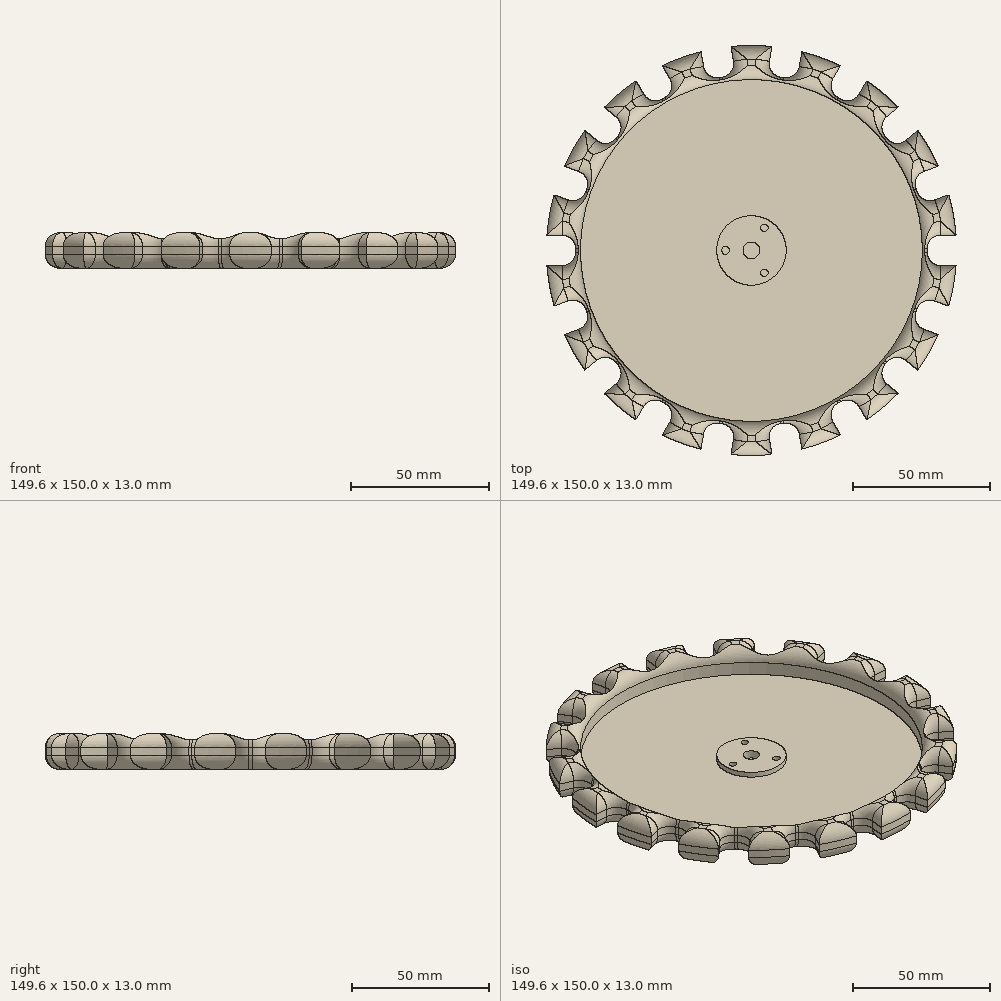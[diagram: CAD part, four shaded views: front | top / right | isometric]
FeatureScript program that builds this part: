
annotation { "Feature Type Name" : "Feature", "Feature Type Description" : "" }
export const myFeature = defineFeature(function(context is Context, id is Id, definition is map)
    precondition{}
    {
        {
            var Q0;
            Q0=qCreatedBy(makeId("Top.planeOp"),FACE);
            var sketch = newSketch(context, id + "F0", { "sketchPlane" : qUnion([Q0])});
            skCircle(sketch, "E0", {"center": v(0, 0) * mm, "radius": 75 * mm});
            skCircle(sketch, "E1", {"center": v(0, 0) * mm, "radius": 62.5 * mm});
            skLineSegment(sketch, "E2", {"start": v(0, 0) * mm, "end": v(-124.02, 0) * mm, "construction": true});
            skPoint(sketch, "E3", {"position": v(-75, 0) * mm});
            skLineSegment(sketch, "E4.bottom", {"start": v(-75.75, -5.55) * mm, "end": v(-69.25, -5.55) * mm});
            skLineSegment(sketch, "E4.top", {"start": v(-75.75, 5.55) * mm, "end": v(-69.25, 5.55) * mm});
            skLineSegment(sketch, "E4.left", {"start": v(-75.75, -5.55) * mm, "end": v(-75.75, 5.55) * mm});
            skLineSegment(sketch, "E4.right", {"start": v(-64.25, -0.55) * mm, "end": v(-64.25, 0.55) * mm});
            skPoint(sketch, "E4.middle", {"position": v(-70, 0) * mm});
            skPoint(sketch, "E5.visualSharp", {"position": v(-64.25, 5.55) * mm});
            skArc(sketch, "E5.filletArc", {"start": v(-64.25, 0.55) * mm, "mid": v(-65.71, 4.09) * mm, "end": v(-69.25, 5.55) * mm});
            skPoint(sketch, "E6.visualSharp", {"position": v(-64.25, -5.55) * mm});
            skArc(sketch, "E6.filletArc", {"start": v(-69.25, -5.55) * mm, "mid": v(-65.71, -4.09) * mm, "end": v(-64.25, -0.55) * mm});
            skPoint(sketch, "E7.center", {"position": v(1.56, 0) * mm});
            skCircle(sketch, "E8", {"center": v(0, 0) * mm, "radius": 3.05 * mm});
            skCircle(sketch, "E9", {"center": v(0, 0) * mm, "radius": 12.7 * mm});
            skCircle(sketch, "E10", {"center": v(0, 0) * mm, "radius": 9.5 * mm, "construction": true});
            skCircle(sketch, "E11", {"center": v(-9.5, 0) * mm, "radius": 1.4 * mm});
            skCircle(sketch, "E12.1.0", {"center": v(-4.75, -8.23) * mm, "radius": 1.4 * mm});
            skCircle(sketch, "E12.2.0", {"center": v(4.75, -8.23) * mm, "radius": 1.4 * mm});
            skCircle(sketch, "E12.3.0", {"center": v(9.5, 0) * mm, "radius": 1.4 * mm});
            skCircle(sketch, "E12.4.0", {"center": v(4.75, 8.23) * mm, "radius": 1.4 * mm});
            skCircle(sketch, "E12.5.0", {"center": v(-4.75, 8.23) * mm, "radius": 1.4 * mm});
            skPoint(sketch, "E13.1.0", {"position": v(-62.27, -16.76) * mm});
            skPoint(sketch, "E13.1.1", {"position": v(-70.48, -25.65) * mm});
            skPoint(sketch, "E13.1.2", {"position": v(-58.48, -27.2) * mm});
            skPoint(sketch, "E13.1.3", {"position": v(-65.78, -23.94) * mm});
            skArc(sketch, "E13.1.4", {"start": v(-63.18, -28.9) * mm, "mid": v(-60.35, -26.31) * mm, "end": v(-60.19, -22.5) * mm});
            skArc(sketch, "E13.1.5", {"start": v(-60.56, -21.46) * mm, "mid": v(-63.15, -18.64) * mm, "end": v(-66.97, -18.47) * mm});
            skLineSegment(sketch, "E13.1.6", {"start": v(-69.28, -31.12) * mm, "end": v(-73.08, -20.7) * mm});
            skLineSegment(sketch, "E13.1.7", {"start": v(-60.19, -22.5) * mm, "end": v(-60.56, -21.46) * mm});
            skLineSegment(sketch, "E13.1.8", {"start": v(-73.08, -20.7) * mm, "end": v(-66.97, -18.47) * mm});
            skLineSegment(sketch, "E13.1.9", {"start": v(-69.28, -31.12) * mm, "end": v(-63.18, -28.9) * mm});
            skPoint(sketch, "E13.2.0", {"position": v(-52.79, -37.05) * mm});
            skPoint(sketch, "E13.2.1", {"position": v(-57.45, -48.2) * mm});
            skPoint(sketch, "E13.2.2", {"position": v(-45.65, -45.55) * mm});
            skPoint(sketch, "E13.2.3", {"position": v(-53.62, -45) * mm});
            skArc(sketch, "E13.2.4", {"start": v(-49.48, -48.76) * mm, "mid": v(-47.71, -45.37) * mm, "end": v(-48.86, -41.72) * mm});
            skArc(sketch, "E13.2.5", {"start": v(-49.57, -40.88) * mm, "mid": v(-52.97, -39.11) * mm, "end": v(-56.62, -40.26) * mm});
            skLineSegment(sketch, "E13.2.6", {"start": v(-54.46, -52.94) * mm, "end": v(-61.6, -44.44) * mm});
            skLineSegment(sketch, "E13.2.7", {"start": v(-48.86, -41.72) * mm, "end": v(-49.57, -40.88) * mm});
            skLineSegment(sketch, "E13.2.8", {"start": v(-61.6, -44.44) * mm, "end": v(-56.62, -40.26) * mm});
            skLineSegment(sketch, "E13.2.9", {"start": v(-54.46, -52.94) * mm, "end": v(-49.48, -48.76) * mm});
            skPoint(sketch, "E13.3.0", {"position": v(-36.93, -52.87) * mm});
            skPoint(sketch, "E13.3.1", {"position": v(-37.5, -64.95) * mm});
            skPoint(sketch, "E13.3.2", {"position": v(-27.32, -58.42) * mm});
            skPoint(sketch, "E13.3.3", {"position": v(-35, -60.62) * mm});
            skArc(sketch, "E13.3.4", {"start": v(-29.82, -62.75) * mm, "mid": v(-29.32, -58.95) * mm, "end": v(-31.65, -55.92) * mm});
            skArc(sketch, "E13.3.5", {"start": v(-32.6, -55.37) * mm, "mid": v(-36.4, -54.87) * mm, "end": v(-39.43, -57.2) * mm});
            skLineSegment(sketch, "E13.3.6", {"start": v(-33.07, -68.38) * mm, "end": v(-42.68, -62.83) * mm});
            skLineSegment(sketch, "E13.3.7", {"start": v(-31.65, -55.92) * mm, "end": v(-32.6, -55.37) * mm});
            skLineSegment(sketch, "E13.3.8", {"start": v(-42.68, -62.83) * mm, "end": v(-39.43, -57.2) * mm});
            skLineSegment(sketch, "E13.3.9", {"start": v(-33.07, -68.38) * mm, "end": v(-29.82, -62.75) * mm});
            skPoint(sketch, "E13.4.0", {"position": v(-16.62, -62.31) * mm});
            skPoint(sketch, "E13.4.1", {"position": v(-13.02, -73.86) * mm});
            skPoint(sketch, "E13.4.2", {"position": v(-5.7, -64.24) * mm});
            skPoint(sketch, "E13.4.3", {"position": v(-12.16, -68.94) * mm});
            skArc(sketch, "E13.4.4", {"start": v(-6.56, -69.16) * mm, "mid": v(-7.39, -65.43) * mm, "end": v(-10.62, -63.37) * mm});
            skArc(sketch, "E13.4.5", {"start": v(-11.7, -63.18) * mm, "mid": v(-15.43, -64) * mm, "end": v(-17.5, -67.23) * mm});
            skLineSegment(sketch, "E13.4.6", {"start": v(-7.69, -75.56) * mm, "end": v(-18.62, -73.64) * mm});
            skLineSegment(sketch, "E13.4.7", {"start": v(-10.62, -63.37) * mm, "end": v(-11.7, -63.18) * mm});
            skLineSegment(sketch, "E13.4.8", {"start": v(-18.62, -73.64) * mm, "end": v(-17.5, -67.23) * mm});
            skLineSegment(sketch, "E13.4.9", {"start": v(-7.69, -75.56) * mm, "end": v(-6.56, -69.16) * mm});
            skPoint(sketch, "E13.5.0", {"position": v(5.7, -64.24) * mm});
            skPoint(sketch, "E13.5.1", {"position": v(13.02, -73.86) * mm});
            skPoint(sketch, "E13.5.2", {"position": v(16.62, -62.31) * mm});
            skPoint(sketch, "E13.5.3", {"position": v(12.16, -68.94) * mm});
            skArc(sketch, "E13.5.4", {"start": v(17.5, -67.23) * mm, "mid": v(15.43, -64) * mm, "end": v(11.7, -63.18) * mm});
            skArc(sketch, "E13.5.5", {"start": v(10.62, -63.37) * mm, "mid": v(7.39, -65.43) * mm, "end": v(6.56, -69.16) * mm});
            skLineSegment(sketch, "E13.5.6", {"start": v(18.62, -73.64) * mm, "end": v(7.69, -75.56) * mm});
            skLineSegment(sketch, "E13.5.7", {"start": v(11.7, -63.18) * mm, "end": v(10.62, -63.37) * mm});
            skLineSegment(sketch, "E13.5.8", {"start": v(7.69, -75.56) * mm, "end": v(6.56, -69.16) * mm});
            skLineSegment(sketch, "E13.5.9", {"start": v(18.62, -73.64) * mm, "end": v(17.5, -67.23) * mm});
            skPoint(sketch, "E13.6.0", {"position": v(27.32, -58.42) * mm});
            skPoint(sketch, "E13.6.1", {"position": v(37.5, -64.95) * mm});
            skPoint(sketch, "E13.6.2", {"position": v(36.93, -52.87) * mm});
            skPoint(sketch, "E13.6.3", {"position": v(35, -60.62) * mm});
            skArc(sketch, "E13.6.4", {"start": v(39.43, -57.2) * mm, "mid": v(36.4, -54.87) * mm, "end": v(32.6, -55.37) * mm});
            skArc(sketch, "E13.6.5", {"start": v(31.65, -55.92) * mm, "mid": v(29.32, -58.95) * mm, "end": v(29.82, -62.75) * mm});
            skLineSegment(sketch, "E13.6.6", {"start": v(42.68, -62.83) * mm, "end": v(33.07, -68.38) * mm});
            skLineSegment(sketch, "E13.6.7", {"start": v(32.6, -55.37) * mm, "end": v(31.65, -55.92) * mm});
            skLineSegment(sketch, "E13.6.8", {"start": v(33.07, -68.38) * mm, "end": v(29.82, -62.75) * mm});
            skLineSegment(sketch, "E13.6.9", {"start": v(42.68, -62.83) * mm, "end": v(39.43, -57.2) * mm});
            skPoint(sketch, "E13.7.0", {"position": v(45.65, -45.55) * mm});
            skPoint(sketch, "E13.7.1", {"position": v(57.45, -48.2) * mm});
            skPoint(sketch, "E13.7.2", {"position": v(52.79, -37.05) * mm});
            skPoint(sketch, "E13.7.3", {"position": v(53.62, -45) * mm});
            skArc(sketch, "E13.7.4", {"start": v(56.62, -40.26) * mm, "mid": v(52.97, -39.11) * mm, "end": v(49.57, -40.88) * mm});
            skArc(sketch, "E13.7.5", {"start": v(48.86, -41.72) * mm, "mid": v(47.71, -45.37) * mm, "end": v(49.48, -48.76) * mm});
            skLineSegment(sketch, "E13.7.6", {"start": v(61.6, -44.44) * mm, "end": v(54.46, -52.94) * mm});
            skLineSegment(sketch, "E13.7.7", {"start": v(49.57, -40.88) * mm, "end": v(48.86, -41.72) * mm});
            skLineSegment(sketch, "E13.7.8", {"start": v(54.46, -52.94) * mm, "end": v(49.48, -48.76) * mm});
            skLineSegment(sketch, "E13.7.9", {"start": v(61.6, -44.44) * mm, "end": v(56.62, -40.26) * mm});
            skPoint(sketch, "E13.8.0", {"position": v(58.48, -27.2) * mm});
            skPoint(sketch, "E13.8.1", {"position": v(70.48, -25.65) * mm});
            skPoint(sketch, "E13.8.2", {"position": v(62.27, -16.76) * mm});
            skPoint(sketch, "E13.8.3", {"position": v(65.78, -23.94) * mm});
            skArc(sketch, "E13.8.4", {"start": v(66.97, -18.47) * mm, "mid": v(63.15, -18.64) * mm, "end": v(60.56, -21.46) * mm});
            skArc(sketch, "E13.8.5", {"start": v(60.19, -22.5) * mm, "mid": v(60.35, -26.31) * mm, "end": v(63.18, -28.9) * mm});
            skLineSegment(sketch, "E13.8.6", {"start": v(73.08, -20.7) * mm, "end": v(69.28, -31.12) * mm});
            skLineSegment(sketch, "E13.8.7", {"start": v(60.56, -21.46) * mm, "end": v(60.19, -22.5) * mm});
            skLineSegment(sketch, "E13.8.8", {"start": v(69.28, -31.12) * mm, "end": v(63.18, -28.9) * mm});
            skLineSegment(sketch, "E13.8.9", {"start": v(73.08, -20.7) * mm, "end": v(66.97, -18.47) * mm});
            skPoint(sketch, "E13.9.0", {"position": v(64.25, -5.55) * mm});
            skPoint(sketch, "E13.9.1", {"position": v(75, 0) * mm});
            skPoint(sketch, "E13.9.2", {"position": v(64.25, 5.55) * mm});
            skPoint(sketch, "E13.9.3", {"position": v(70, 0) * mm});
            skArc(sketch, "E13.9.4", {"start": v(69.25, 5.55) * mm, "mid": v(65.71, 4.09) * mm, "end": v(64.25, 0.55) * mm});
            skArc(sketch, "E13.9.5", {"start": v(64.25, -0.55) * mm, "mid": v(65.71, -4.09) * mm, "end": v(69.25, -5.55) * mm});
            skLineSegment(sketch, "E13.9.6", {"start": v(75.75, 5.55) * mm, "end": v(75.75, -5.55) * mm});
            skLineSegment(sketch, "E13.9.7", {"start": v(64.25, 0.55) * mm, "end": v(64.25, -0.55) * mm});
            skLineSegment(sketch, "E13.9.8", {"start": v(75.75, -5.55) * mm, "end": v(69.25, -5.55) * mm});
            skLineSegment(sketch, "E13.9.9", {"start": v(75.75, 5.55) * mm, "end": v(69.25, 5.55) * mm});
            skPoint(sketch, "E13.10.0", {"position": v(62.27, 16.76) * mm});
            skPoint(sketch, "E13.10.1", {"position": v(70.48, 25.65) * mm});
            skPoint(sketch, "E13.10.2", {"position": v(58.48, 27.2) * mm});
            skPoint(sketch, "E13.10.3", {"position": v(65.78, 23.94) * mm});
            skArc(sketch, "E13.10.4", {"start": v(63.18, 28.9) * mm, "mid": v(60.35, 26.31) * mm, "end": v(60.19, 22.5) * mm});
            skArc(sketch, "E13.10.5", {"start": v(60.56, 21.46) * mm, "mid": v(63.15, 18.64) * mm, "end": v(66.97, 18.47) * mm});
            skLineSegment(sketch, "E13.10.6", {"start": v(69.28, 31.12) * mm, "end": v(73.08, 20.7) * mm});
            skLineSegment(sketch, "E13.10.7", {"start": v(60.19, 22.5) * mm, "end": v(60.56, 21.46) * mm});
            skLineSegment(sketch, "E13.10.8", {"start": v(73.08, 20.7) * mm, "end": v(66.97, 18.47) * mm});
            skLineSegment(sketch, "E13.10.9", {"start": v(69.28, 31.12) * mm, "end": v(63.18, 28.9) * mm});
            skPoint(sketch, "E13.11.0", {"position": v(52.79, 37.05) * mm});
            skPoint(sketch, "E13.11.1", {"position": v(57.45, 48.2) * mm});
            skPoint(sketch, "E13.11.2", {"position": v(45.65, 45.55) * mm});
            skPoint(sketch, "E13.11.3", {"position": v(53.62, 45) * mm});
            skArc(sketch, "E13.11.4", {"start": v(49.48, 48.76) * mm, "mid": v(47.71, 45.37) * mm, "end": v(48.86, 41.72) * mm});
            skArc(sketch, "E13.11.5", {"start": v(49.57, 40.88) * mm, "mid": v(52.97, 39.11) * mm, "end": v(56.62, 40.26) * mm});
            skLineSegment(sketch, "E13.11.6", {"start": v(54.46, 52.94) * mm, "end": v(61.6, 44.44) * mm});
            skLineSegment(sketch, "E13.11.7", {"start": v(48.86, 41.72) * mm, "end": v(49.57, 40.88) * mm});
            skLineSegment(sketch, "E13.11.8", {"start": v(61.6, 44.44) * mm, "end": v(56.62, 40.26) * mm});
            skLineSegment(sketch, "E13.11.9", {"start": v(54.46, 52.94) * mm, "end": v(49.48, 48.76) * mm});
            skPoint(sketch, "E13.12.0", {"position": v(36.93, 52.87) * mm});
            skPoint(sketch, "E13.12.1", {"position": v(37.5, 64.95) * mm});
            skPoint(sketch, "E13.12.2", {"position": v(27.32, 58.42) * mm});
            skPoint(sketch, "E13.12.3", {"position": v(35, 60.62) * mm});
            skArc(sketch, "E13.12.4", {"start": v(29.82, 62.75) * mm, "mid": v(29.32, 58.95) * mm, "end": v(31.65, 55.92) * mm});
            skArc(sketch, "E13.12.5", {"start": v(32.6, 55.37) * mm, "mid": v(36.4, 54.87) * mm, "end": v(39.43, 57.2) * mm});
            skLineSegment(sketch, "E13.12.6", {"start": v(33.07, 68.38) * mm, "end": v(42.68, 62.83) * mm});
            skLineSegment(sketch, "E13.12.7", {"start": v(31.65, 55.92) * mm, "end": v(32.6, 55.37) * mm});
            skLineSegment(sketch, "E13.12.8", {"start": v(42.68, 62.83) * mm, "end": v(39.43, 57.2) * mm});
            skLineSegment(sketch, "E13.12.9", {"start": v(33.07, 68.38) * mm, "end": v(29.82, 62.75) * mm});
            skPoint(sketch, "E13.13.0", {"position": v(16.62, 62.31) * mm});
            skPoint(sketch, "E13.13.1", {"position": v(13.02, 73.86) * mm});
            skPoint(sketch, "E13.13.2", {"position": v(5.7, 64.24) * mm});
            skPoint(sketch, "E13.13.3", {"position": v(12.16, 68.94) * mm});
            skArc(sketch, "E13.13.4", {"start": v(6.56, 69.16) * mm, "mid": v(7.39, 65.43) * mm, "end": v(10.62, 63.37) * mm});
            skArc(sketch, "E13.13.5", {"start": v(11.7, 63.18) * mm, "mid": v(15.43, 64) * mm, "end": v(17.5, 67.23) * mm});
            skLineSegment(sketch, "E13.13.6", {"start": v(7.69, 75.56) * mm, "end": v(18.62, 73.64) * mm});
            skLineSegment(sketch, "E13.13.7", {"start": v(10.62, 63.37) * mm, "end": v(11.7, 63.18) * mm});
            skLineSegment(sketch, "E13.13.8", {"start": v(18.62, 73.64) * mm, "end": v(17.5, 67.23) * mm});
            skLineSegment(sketch, "E13.13.9", {"start": v(7.69, 75.56) * mm, "end": v(6.56, 69.16) * mm});
            skPoint(sketch, "E13.14.0", {"position": v(-5.7, 64.24) * mm});
            skPoint(sketch, "E13.14.1", {"position": v(-13.02, 73.86) * mm});
            skPoint(sketch, "E13.14.2", {"position": v(-16.62, 62.31) * mm});
            skPoint(sketch, "E13.14.3", {"position": v(-12.16, 68.94) * mm});
            skArc(sketch, "E13.14.4", {"start": v(-17.5, 67.23) * mm, "mid": v(-15.43, 64) * mm, "end": v(-11.7, 63.18) * mm});
            skArc(sketch, "E13.14.5", {"start": v(-10.62, 63.37) * mm, "mid": v(-7.39, 65.43) * mm, "end": v(-6.56, 69.16) * mm});
            skLineSegment(sketch, "E13.14.6", {"start": v(-18.62, 73.64) * mm, "end": v(-7.69, 75.56) * mm});
            skLineSegment(sketch, "E13.14.7", {"start": v(-11.7, 63.18) * mm, "end": v(-10.62, 63.37) * mm});
            skLineSegment(sketch, "E13.14.8", {"start": v(-7.69, 75.56) * mm, "end": v(-6.56, 69.16) * mm});
            skLineSegment(sketch, "E13.14.9", {"start": v(-18.62, 73.64) * mm, "end": v(-17.5, 67.23) * mm});
            skPoint(sketch, "E13.15.0", {"position": v(-27.32, 58.42) * mm});
            skPoint(sketch, "E13.15.1", {"position": v(-37.5, 64.95) * mm});
            skPoint(sketch, "E13.15.2", {"position": v(-36.93, 52.87) * mm});
            skPoint(sketch, "E13.15.3", {"position": v(-35, 60.62) * mm});
            skArc(sketch, "E13.15.4", {"start": v(-39.43, 57.2) * mm, "mid": v(-36.4, 54.87) * mm, "end": v(-32.6, 55.37) * mm});
            skArc(sketch, "E13.15.5", {"start": v(-31.65, 55.92) * mm, "mid": v(-29.32, 58.95) * mm, "end": v(-29.82, 62.75) * mm});
            skLineSegment(sketch, "E13.15.6", {"start": v(-42.68, 62.83) * mm, "end": v(-33.07, 68.38) * mm});
            skLineSegment(sketch, "E13.15.7", {"start": v(-32.6, 55.37) * mm, "end": v(-31.65, 55.92) * mm});
            skLineSegment(sketch, "E13.15.8", {"start": v(-33.07, 68.38) * mm, "end": v(-29.82, 62.75) * mm});
            skLineSegment(sketch, "E13.15.9", {"start": v(-42.68, 62.83) * mm, "end": v(-39.43, 57.2) * mm});
            skPoint(sketch, "E13.16.0", {"position": v(-45.65, 45.55) * mm});
            skPoint(sketch, "E13.16.1", {"position": v(-57.45, 48.2) * mm});
            skPoint(sketch, "E13.16.2", {"position": v(-52.79, 37.05) * mm});
            skPoint(sketch, "E13.16.3", {"position": v(-53.62, 45) * mm});
            skArc(sketch, "E13.16.4", {"start": v(-56.62, 40.26) * mm, "mid": v(-52.97, 39.11) * mm, "end": v(-49.57, 40.88) * mm});
            skArc(sketch, "E13.16.5", {"start": v(-48.86, 41.72) * mm, "mid": v(-47.71, 45.37) * mm, "end": v(-49.48, 48.76) * mm});
            skLineSegment(sketch, "E13.16.6", {"start": v(-61.6, 44.44) * mm, "end": v(-54.46, 52.94) * mm});
            skLineSegment(sketch, "E13.16.7", {"start": v(-49.57, 40.88) * mm, "end": v(-48.86, 41.72) * mm});
            skLineSegment(sketch, "E13.16.8", {"start": v(-54.46, 52.94) * mm, "end": v(-49.48, 48.76) * mm});
            skLineSegment(sketch, "E13.16.9", {"start": v(-61.6, 44.44) * mm, "end": v(-56.62, 40.26) * mm});
            skPoint(sketch, "E13.17.0", {"position": v(-58.48, 27.2) * mm});
            skPoint(sketch, "E13.17.1", {"position": v(-70.48, 25.65) * mm});
            skPoint(sketch, "E13.17.2", {"position": v(-62.27, 16.76) * mm});
            skPoint(sketch, "E13.17.3", {"position": v(-65.78, 23.94) * mm});
            skArc(sketch, "E13.17.4", {"start": v(-66.97, 18.47) * mm, "mid": v(-63.15, 18.64) * mm, "end": v(-60.56, 21.46) * mm});
            skArc(sketch, "E13.17.5", {"start": v(-60.19, 22.5) * mm, "mid": v(-60.35, 26.31) * mm, "end": v(-63.18, 28.9) * mm});
            skLineSegment(sketch, "E13.17.6", {"start": v(-73.08, 20.7) * mm, "end": v(-69.28, 31.12) * mm});
            skLineSegment(sketch, "E13.17.7", {"start": v(-60.56, 21.46) * mm, "end": v(-60.19, 22.5) * mm});
            skLineSegment(sketch, "E13.17.8", {"start": v(-69.28, 31.12) * mm, "end": v(-63.18, 28.9) * mm});
            skLineSegment(sketch, "E13.17.9", {"start": v(-73.08, 20.7) * mm, "end": v(-66.97, 18.47) * mm});
            skSolve(sketch);
        }
        {
            var Q0;
            Q0=makeQuery(id+"F0.imprint","IMPRINT",FACE,{"disambiguationData":[TD([[makeQuery(id+"F0.imprint","IMPRINT",EDGE,{"derivedFrom":sQuery(id+"F0.wireOp",EDGE,"E1")}),1.0]])]});
            var Q1;
            Q1=makeQuery(id+"F0.imprint","IMPRINT",FACE,{"disambiguationData":[TD([[makeQuery(id+"F0.imprint","IMPRINT",EDGE,{"derivedFrom":sQuery(id+"F0.wireOp",EDGE,"E8")}),-1.0]])]});
            var Q2;
            Q2=makeQuery(id+"F0.imprint","IMPRINT",FACE,{"disambiguationData":[TD([[makeQuery(id+"F0.imprint","IMPRINT",EDGE,{"derivedFrom":sQuery(id+"F0.wireOp",EDGE,"E12.3.0")}),1.0]])]});
            var Q3;
            Q3=makeQuery(id+"F0.imprint","IMPRINT",FACE,{"disambiguationData":[TD([[makeQuery(id+"F0.imprint","IMPRINT",EDGE,{"derivedFrom":sQuery(id+"F0.wireOp",EDGE,"E12.4.0")}),1.0]])]});
            var Q4;
            Q4=makeQuery(id+"F0.imprint","IMPRINT",FACE,{"disambiguationData":[TD([[makeQuery(id+"F0.imprint","IMPRINT",EDGE,{"derivedFrom":sQuery(id+"F0.wireOp",EDGE,"E12.5.0")}),1.0]])]});
            var Q5;
            Q5=makeQuery(id+"F0.imprint","IMPRINT",FACE,{"disambiguationData":[TD([[makeQuery(id+"F0.imprint","IMPRINT",EDGE,{"derivedFrom":sQuery(id+"F0.wireOp",EDGE,"E11")}),1.0]])]});
            var Q6;
            Q6=makeQuery(id+"F0.imprint","IMPRINT",FACE,{"disambiguationData":[TD([[makeQuery(id+"F0.imprint","IMPRINT",EDGE,{"derivedFrom":sQuery(id+"F0.wireOp",EDGE,"E12.1.0")}),1.0]])]});
            var Q7;
            Q7=makeQuery(id+"F0.imprint","IMPRINT",FACE,{"disambiguationData":[TD([[makeQuery(id+"F0.imprint","IMPRINT",EDGE,{"derivedFrom":sQuery(id+"F0.wireOp",EDGE,"E12.2.0")}),1.0]])]});
            extrude(context, id + "F1", {"entities" : qUnion([Q0, Q1, Q2, Q3, Q4, Q5, Q6, Q7]), "depth" : 3 * mm, "offsetDistance" : 25 * mm});
        }
        {
            var Q0;
            Q0=makeQuery(id+"F0.imprint","IMPRINT",FACE,{"disambiguationData":[TD([[makeQuery(id+"F0.imprint","IMPRINT",EDGE,{"derivedFrom":sQuery(id+"F0.wireOp",EDGE,"E1")}),-1.0]])]});
            extrude(context, id + "F2", {"entities" : qUnion([Q0]), "operationType" : NewBodyOperationType.ADD, "depth" : 13 * mm, "offsetDistance" : 25 * mm});
        }
        {
            var Q0;
            Q0=makeQuery(id+"F0.imprint","IMPRINT",FACE,{"disambiguationData":[TD([[makeQuery(id+"F0.imprint","IMPRINT",EDGE,{"derivedFrom":sQuery(id+"F0.wireOp",EDGE,"E8")}),-1.0]])]});
            var Q1;
            Q1=makeQuery(id+"F0.imprint","IMPRINT",FACE,{"disambiguationData":[TD([[makeQuery(id+"F0.imprint","IMPRINT",EDGE,{"derivedFrom":sQuery(id+"F0.wireOp",EDGE,"E12.5.0")}),1.0]])]});
            var Q2;
            Q2=makeQuery(id+"F0.imprint","IMPRINT",FACE,{"disambiguationData":[TD([[makeQuery(id+"F0.imprint","IMPRINT",EDGE,{"derivedFrom":sQuery(id+"F0.wireOp",EDGE,"E12.3.0")}),1.0]])]});
            var Q3;
            Q3=makeQuery(id+"F0.imprint","IMPRINT",FACE,{"disambiguationData":[TD([[makeQuery(id+"F0.imprint","IMPRINT",EDGE,{"derivedFrom":sQuery(id+"F0.wireOp",EDGE,"E12.1.0")}),1.0]])]});
            extrude(context, id + "F3", {"entities" : qUnion([Q0, Q1, Q2, Q3]), "operationType" : NewBodyOperationType.ADD, "depth" : 5 * mm, "offsetDistance" : 25 * mm});
        }
        {
            var Q0;
            Q0=makeQuery(id+"F0.imprint","IMPRINT",FACE,{"disambiguationData":[TD([[makeQuery(id+"F0.imprint","IMPRINT",EDGE,{"derivedFrom":sQuery(id+"F0.wireOp",EDGE,"E8")}),1.0]])]});
            extrude(context, id + "F4", {"entities" : qUnion([Q0]), "operationType" : NewBodyOperationType.ADD, "depth" : 2 * mm, "offsetDistance" : 25 * mm});
        }
        {
            var Q0;
            {var subQ0=sQuery(id+"F0.wireOp",EDGE,"E8");var subQ1=sQuery(id+"F0.wireOp",EDGE,"E1");Q0=makeQuery(id+"F4.boolean.opBoolean","MERGE",FACE,{"derivedFrom":[makeQuery(id+"F2.boolean.opBoolean","MERGE",FACE,{"derivedFrom":[makeQuery(id+"F1.opExtrude","CAP_FACE",FACE,{"disambiguationData":[OSD([subQ1,subQ0])],"isStart":true}),makeQuery(id+"F2.opExtrude","CAP_FACE",FACE,{"disambiguationData":[OSD([sQuery(id+"F0.wireOp",EDGE,"E0"),subQ1,sQuery(id+"F0.wireOp",EDGE,"E4.bottom"),sQuery(id+"F0.wireOp",EDGE,"E4.top"),sQuery(id+"F0.wireOp",EDGE,"E4.right"),sQuery(id+"F0.wireOp",EDGE,"E5.filletArc"),sQuery(id+"F0.wireOp",EDGE,"E6.filletArc"),sQuery(id+"F0.wireOp",EDGE,"E13.1.4"),sQuery(id+"F0.wireOp",EDGE,"E13.1.5"),sQuery(id+"F0.wireOp",EDGE,"E13.1.7"),sQuery(id+"F0.wireOp",EDGE,"E13.1.8"),sQuery(id+"F0.wireOp",EDGE,"E13.1.9"),sQuery(id+"F0.wireOp",EDGE,"E13.2.4"),sQuery(id+"F0.wireOp",EDGE,"E13.2.5"),sQuery(id+"F0.wireOp",EDGE,"E13.2.7"),sQuery(id+"F0.wireOp",EDGE,"E13.2.8"),sQuery(id+"F0.wireOp",EDGE,"E13.2.9"),sQuery(id+"F0.wireOp",EDGE,"E13.3.4"),sQuery(id+"F0.wireOp",EDGE,"E13.3.5"),sQuery(id+"F0.wireOp",EDGE,"E13.3.7"),sQuery(id+"F0.wireOp",EDGE,"E13.3.8"),sQuery(id+"F0.wireOp",EDGE,"E13.3.9"),sQuery(id+"F0.wireOp",EDGE,"E13.4.4"),sQuery(id+"F0.wireOp",EDGE,"E13.4.5"),sQuery(id+"F0.wireOp",EDGE,"E13.4.7"),sQuery(id+"F0.wireOp",EDGE,"E13.4.8"),sQuery(id+"F0.wireOp",EDGE,"E13.4.9"),sQuery(id+"F0.wireOp",EDGE,"E13.5.4"),sQuery(id+"F0.wireOp",EDGE,"E13.5.5"),sQuery(id+"F0.wireOp",EDGE,"E13.5.7"),sQuery(id+"F0.wireOp",EDGE,"E13.5.8"),sQuery(id+"F0.wireOp",EDGE,"E13.5.9"),sQuery(id+"F0.wireOp",EDGE,"E13.6.4"),sQuery(id+"F0.wireOp",EDGE,"E13.6.5"),sQuery(id+"F0.wireOp",EDGE,"E13.6.7"),sQuery(id+"F0.wireOp",EDGE,"E13.6.8"),sQuery(id+"F0.wireOp",EDGE,"E13.6.9"),sQuery(id+"F0.wireOp",EDGE,"E13.7.4"),sQuery(id+"F0.wireOp",EDGE,"E13.7.5"),sQuery(id+"F0.wireOp",EDGE,"E13.7.7"),sQuery(id+"F0.wireOp",EDGE,"E13.7.8"),sQuery(id+"F0.wireOp",EDGE,"E13.7.9"),sQuery(id+"F0.wireOp",EDGE,"E13.8.4"),sQuery(id+"F0.wireOp",EDGE,"E13.8.5"),sQuery(id+"F0.wireOp",EDGE,"E13.8.7"),sQuery(id+"F0.wireOp",EDGE,"E13.8.8"),sQuery(id+"F0.wireOp",EDGE,"E13.8.9"),sQuery(id+"F0.wireOp",EDGE,"E13.9.4"),sQuery(id+"F0.wireOp",EDGE,"E13.9.5"),sQuery(id+"F0.wireOp",EDGE,"E13.9.7"),sQuery(id+"F0.wireOp",EDGE,"E13.9.8"),sQuery(id+"F0.wireOp",EDGE,"E13.9.9"),sQuery(id+"F0.wireOp",EDGE,"E13.10.4"),sQuery(id+"F0.wireOp",EDGE,"E13.10.5"),sQuery(id+"F0.wireOp",EDGE,"E13.10.7"),sQuery(id+"F0.wireOp",EDGE,"E13.10.8"),sQuery(id+"F0.wireOp",EDGE,"E13.10.9"),sQuery(id+"F0.wireOp",EDGE,"E13.11.4"),sQuery(id+"F0.wireOp",EDGE,"E13.11.5"),sQuery(id+"F0.wireOp",EDGE,"E13.11.7"),sQuery(id+"F0.wireOp",EDGE,"E13.11.8"),sQuery(id+"F0.wireOp",EDGE,"E13.11.9"),sQuery(id+"F0.wireOp",EDGE,"E13.12.4"),sQuery(id+"F0.wireOp",EDGE,"E13.12.5"),sQuery(id+"F0.wireOp",EDGE,"E13.12.7"),sQuery(id+"F0.wireOp",EDGE,"E13.12.8"),sQuery(id+"F0.wireOp",EDGE,"E13.12.9"),sQuery(id+"F0.wireOp",EDGE,"E13.13.4"),sQuery(id+"F0.wireOp",EDGE,"E13.13.5"),sQuery(id+"F0.wireOp",EDGE,"E13.13.7"),sQuery(id+"F0.wireOp",EDGE,"E13.13.8"),sQuery(id+"F0.wireOp",EDGE,"E13.13.9"),sQuery(id+"F0.wireOp",EDGE,"E13.14.4"),sQuery(id+"F0.wireOp",EDGE,"E13.14.5"),sQuery(id+"F0.wireOp",EDGE,"E13.14.7"),sQuery(id+"F0.wireOp",EDGE,"E13.14.8"),sQuery(id+"F0.wireOp",EDGE,"E13.14.9"),sQuery(id+"F0.wireOp",EDGE,"E13.15.4"),sQuery(id+"F0.wireOp",EDGE,"E13.15.5"),sQuery(id+"F0.wireOp",EDGE,"E13.15.7"),sQuery(id+"F0.wireOp",EDGE,"E13.15.8"),sQuery(id+"F0.wireOp",EDGE,"E13.15.9"),sQuery(id+"F0.wireOp",EDGE,"E13.16.4"),sQuery(id+"F0.wireOp",EDGE,"E13.16.5"),sQuery(id+"F0.wireOp",EDGE,"E13.16.7"),sQuery(id+"F0.wireOp",EDGE,"E13.16.8"),sQuery(id+"F0.wireOp",EDGE,"E13.16.9"),sQuery(id+"F0.wireOp",EDGE,"E13.17.4"),sQuery(id+"F0.wireOp",EDGE,"E13.17.5"),sQuery(id+"F0.wireOp",EDGE,"E13.17.7"),sQuery(id+"F0.wireOp",EDGE,"E13.17.8"),sQuery(id+"F0.wireOp",EDGE,"E13.17.9")])],"isStart":true})]}),makeQuery(id+"F4.opExtrude","CAP_FACE",FACE,{"disambiguationData":[OSD([subQ0])],"isStart":true})]});}
            var Q1;
            Q1=makeQuery(id+"F2.opExtrude","CAP_FACE",FACE,{"disambiguationData":[OSD([sQuery(id+"F0.wireOp",EDGE,"E0"),sQuery(id+"F0.wireOp",EDGE,"E1"),sQuery(id+"F0.wireOp",EDGE,"E4.bottom"),sQuery(id+"F0.wireOp",EDGE,"E4.top"),sQuery(id+"F0.wireOp",EDGE,"E4.right"),sQuery(id+"F0.wireOp",EDGE,"E5.filletArc"),sQuery(id+"F0.wireOp",EDGE,"E6.filletArc"),sQuery(id+"F0.wireOp",EDGE,"E13.1.4"),sQuery(id+"F0.wireOp",EDGE,"E13.1.5"),sQuery(id+"F0.wireOp",EDGE,"E13.1.7"),sQuery(id+"F0.wireOp",EDGE,"E13.1.8"),sQuery(id+"F0.wireOp",EDGE,"E13.1.9"),sQuery(id+"F0.wireOp",EDGE,"E13.2.4"),sQuery(id+"F0.wireOp",EDGE,"E13.2.5"),sQuery(id+"F0.wireOp",EDGE,"E13.2.7"),sQuery(id+"F0.wireOp",EDGE,"E13.2.8"),sQuery(id+"F0.wireOp",EDGE,"E13.2.9"),sQuery(id+"F0.wireOp",EDGE,"E13.3.4"),sQuery(id+"F0.wireOp",EDGE,"E13.3.5"),sQuery(id+"F0.wireOp",EDGE,"E13.3.7"),sQuery(id+"F0.wireOp",EDGE,"E13.3.8"),sQuery(id+"F0.wireOp",EDGE,"E13.3.9"),sQuery(id+"F0.wireOp",EDGE,"E13.4.4"),sQuery(id+"F0.wireOp",EDGE,"E13.4.5"),sQuery(id+"F0.wireOp",EDGE,"E13.4.7"),sQuery(id+"F0.wireOp",EDGE,"E13.4.8"),sQuery(id+"F0.wireOp",EDGE,"E13.4.9"),sQuery(id+"F0.wireOp",EDGE,"E13.5.4"),sQuery(id+"F0.wireOp",EDGE,"E13.5.5"),sQuery(id+"F0.wireOp",EDGE,"E13.5.7"),sQuery(id+"F0.wireOp",EDGE,"E13.5.8"),sQuery(id+"F0.wireOp",EDGE,"E13.5.9"),sQuery(id+"F0.wireOp",EDGE,"E13.6.4"),sQuery(id+"F0.wireOp",EDGE,"E13.6.5"),sQuery(id+"F0.wireOp",EDGE,"E13.6.7"),sQuery(id+"F0.wireOp",EDGE,"E13.6.8"),sQuery(id+"F0.wireOp",EDGE,"E13.6.9"),sQuery(id+"F0.wireOp",EDGE,"E13.7.4"),sQuery(id+"F0.wireOp",EDGE,"E13.7.5"),sQuery(id+"F0.wireOp",EDGE,"E13.7.7"),sQuery(id+"F0.wireOp",EDGE,"E13.7.8"),sQuery(id+"F0.wireOp",EDGE,"E13.7.9"),sQuery(id+"F0.wireOp",EDGE,"E13.8.4"),sQuery(id+"F0.wireOp",EDGE,"E13.8.5"),sQuery(id+"F0.wireOp",EDGE,"E13.8.7"),sQuery(id+"F0.wireOp",EDGE,"E13.8.8"),sQuery(id+"F0.wireOp",EDGE,"E13.8.9"),sQuery(id+"F0.wireOp",EDGE,"E13.9.4"),sQuery(id+"F0.wireOp",EDGE,"E13.9.5"),sQuery(id+"F0.wireOp",EDGE,"E13.9.7"),sQuery(id+"F0.wireOp",EDGE,"E13.9.8"),sQuery(id+"F0.wireOp",EDGE,"E13.9.9"),sQuery(id+"F0.wireOp",EDGE,"E13.10.4"),sQuery(id+"F0.wireOp",EDGE,"E13.10.5"),sQuery(id+"F0.wireOp",EDGE,"E13.10.7"),sQuery(id+"F0.wireOp",EDGE,"E13.10.8"),sQuery(id+"F0.wireOp",EDGE,"E13.10.9"),sQuery(id+"F0.wireOp",EDGE,"E13.11.4"),sQuery(id+"F0.wireOp",EDGE,"E13.11.5"),sQuery(id+"F0.wireOp",EDGE,"E13.11.7"),sQuery(id+"F0.wireOp",EDGE,"E13.11.8"),sQuery(id+"F0.wireOp",EDGE,"E13.11.9"),sQuery(id+"F0.wireOp",EDGE,"E13.12.4"),sQuery(id+"F0.wireOp",EDGE,"E13.12.5"),sQuery(id+"F0.wireOp",EDGE,"E13.12.7"),sQuery(id+"F0.wireOp",EDGE,"E13.12.8"),sQuery(id+"F0.wireOp",EDGE,"E13.12.9"),sQuery(id+"F0.wireOp",EDGE,"E13.13.4"),sQuery(id+"F0.wireOp",EDGE,"E13.13.5"),sQuery(id+"F0.wireOp",EDGE,"E13.13.7"),sQuery(id+"F0.wireOp",EDGE,"E13.13.8"),sQuery(id+"F0.wireOp",EDGE,"E13.13.9"),sQuery(id+"F0.wireOp",EDGE,"E13.14.4"),sQuery(id+"F0.wireOp",EDGE,"E13.14.5"),sQuery(id+"F0.wireOp",EDGE,"E13.14.7"),sQuery(id+"F0.wireOp",EDGE,"E13.14.8"),sQuery(id+"F0.wireOp",EDGE,"E13.14.9"),sQuery(id+"F0.wireOp",EDGE,"E13.15.4"),sQuery(id+"F0.wireOp",EDGE,"E13.15.5"),sQuery(id+"F0.wireOp",EDGE,"E13.15.7"),sQuery(id+"F0.wireOp",EDGE,"E13.15.8"),sQuery(id+"F0.wireOp",EDGE,"E13.15.9"),sQuery(id+"F0.wireOp",EDGE,"E13.16.4"),sQuery(id+"F0.wireOp",EDGE,"E13.16.5"),sQuery(id+"F0.wireOp",EDGE,"E13.16.7"),sQuery(id+"F0.wireOp",EDGE,"E13.16.8"),sQuery(id+"F0.wireOp",EDGE,"E13.16.9"),sQuery(id+"F0.wireOp",EDGE,"E13.17.4"),sQuery(id+"F0.wireOp",EDGE,"E13.17.5"),sQuery(id+"F0.wireOp",EDGE,"E13.17.7"),sQuery(id+"F0.wireOp",EDGE,"E13.17.8"),sQuery(id+"F0.wireOp",EDGE,"E13.17.9")])],"isStart":false});
            fillet(context, id + "F5", {"entities" : qUnion([Q0, Q1]), "radius" : 5 * mm, "tangentPropagation" : true, "allowEdgeOverflow" : false});
        }
    });
